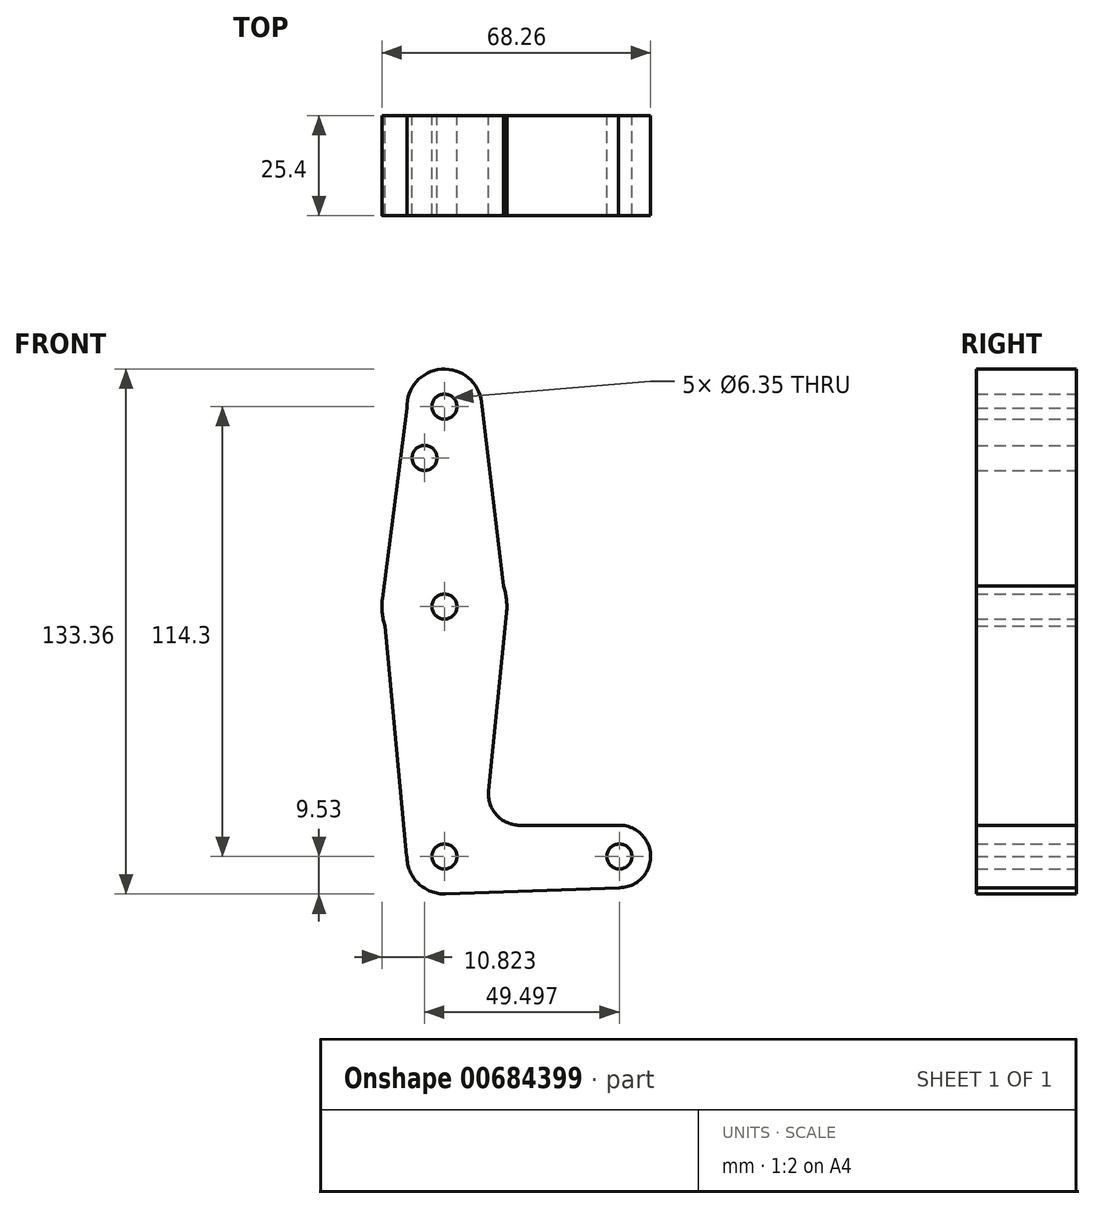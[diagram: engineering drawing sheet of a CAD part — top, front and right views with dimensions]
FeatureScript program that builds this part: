
annotation { "Feature Type Name" : "Feature", "Feature Type Description" : "" }
export const myFeature = defineFeature(function(context is Context, id is Id, definition is map)
    precondition{}
    {
        {
            var Q0;
            Q0=qCreatedBy(makeId("Front.planeOp"),FACE);
            var sketch = newSketch(context, id + "F0", { "sketchPlane" : qUnion([Q0])});
            skCircle(sketch, "E0", {"center": v(0, 0) * mm, "radius": 9.53 * mm});
            skCircle(sketch, "E1", {"center": v(0, 63.5) * mm, "radius": 15.88 * mm});
            skCircle(sketch, "E2", {"center": v(0, 114.3) * mm, "radius": 9.53 * mm});
            skCircle(sketch, "E3", {"center": v(44.45, 0) * mm, "radius": 7.94 * mm});
            skLineSegment(sketch, "E4", {"start": v(0, 63.5) * mm, "end": v(0, 114.3) * mm});
            skLineSegment(sketch, "E5", {"start": v(0, 0) * mm, "end": v(0, 3.18) * mm});
            skLineSegment(sketch, "E6", {"start": v(44.45, 0) * mm, "end": v(0, 0) * mm});
            skLineSegment(sketch, "E7", {"start": v(-9.52, 113.9) * mm, "end": v(-15.74, 65.53) * mm});
            skLineSegment(sketch, "E8", {"start": v(-15.74, 65.53) * mm, "end": v(-9.57, 0) * mm});
            skLineSegment(sketch, "E9", {"start": v(-9.57, 0) * mm, "end": v(3.18, 0) * mm});
            skLineSegment(sketch, "E10", {"start": v(11.21, 16.68) * mm, "end": v(15.8, 61.9) * mm});
            skLineSegment(sketch, "E11", {"start": v(15.8, 61.9) * mm, "end": v(9.46, 115.42) * mm});
            skLineSegment(sketch, "E12", {"start": v(44.17, 7.93) * mm, "end": v(19.12, 7.93) * mm});
            skLineSegment(sketch, "E13", {"start": v(44.45, -7.94) * mm, "end": v(0, -9.53) * mm});
            skCircle(sketch, "E14", {"center": v(0, 114.3) * mm, "radius": 3.18 * mm});
            skCircle(sketch, "E15", {"center": v(-5.05, 101.26) * mm, "radius": 3.18 * mm});
            skCircle(sketch, "E16", {"center": v(0, 63.5) * mm, "radius": 3.18 * mm});
            skCircle(sketch, "E17", {"center": v(0, 0) * mm, "radius": 3.18 * mm});
            skCircle(sketch, "E18", {"center": v(44.45, 0) * mm, "radius": 3.18 * mm});
            skPoint(sketch, "E19.newPointB", {"position": v(0, 7.93) * mm});
            skArc(sketch, "E19.filletArc", {"start": v(11.21, 16.68) * mm, "mid": v(13.23, 10.55) * mm, "end": v(19.12, 7.93) * mm});
            skLineSegment(sketch, "E20.trimOffspring", {"start": v(0, 7.93) * mm, "end": v(0, 63.5) * mm});
            skSolve(sketch);
        }
        {
            var Q0;
            Q0 = qSketchRegion(id + "F0", true);
            extrude(context, id + "F1", {"entities" : qUnion([Q0]), "depth" : 25.4 * mm, "offsetDistance" : 25.4 * mm});
        }
    });
